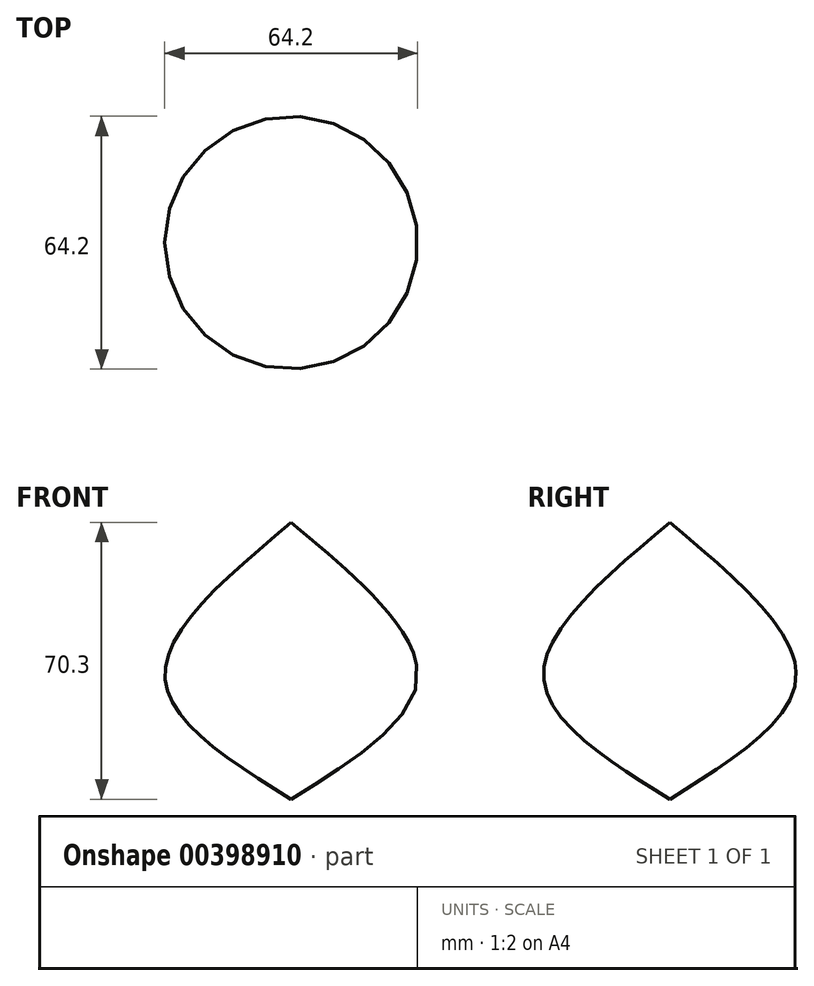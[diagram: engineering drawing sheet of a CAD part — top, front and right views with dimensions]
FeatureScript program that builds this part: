
annotation { "Feature Type Name" : "Feature", "Feature Type Description" : "" }
export const myFeature = defineFeature(function(context is Context, id is Id, definition is map)
    precondition{}
    {
        {
            var Q0;
            Q0=qCreatedBy(makeId("Front.planeOp"),FACE);
            var sketch = newSketch(context, id + "F0", { "sketchPlane" : qUnion([Q0])});
            skLineSegment(sketch, "E0", {"start": v(0, 35.5) * mm, "end": v(0, -34.8) * mm});
            skFitSpline(sketch, "E1", {"points": [v(0, 35.5) * mm, v(-32.08, -3.97) * mm, v(0, -34.8) * mm], "startDerivative": vector(-95.26, -79.66) * mm, "endDerivative": vector(97.41, -60.73) * mm});
            skSolve(sketch);
        }
        {
            var Q0;
            Q0=makeQuery(id+"F0.imprint","IMPRINT",FACE,{"disambiguationData":[TD([[makeQuery(id+"F0.imprint","IMPRINT",EDGE,{"derivedFrom":sQuery(id+"F0.wireOp",EDGE,"E0")}),-1.0]])]});
            var Q1;
            Q1=sQuery(id+"F0.wireOp",EDGE,"E0");
            revolve(context, id + "F1", {"entities" : qUnion([Q0]), "axis" : qUnion([Q1]), "revolveType" : RevolveType.FULL});
        }
    });
